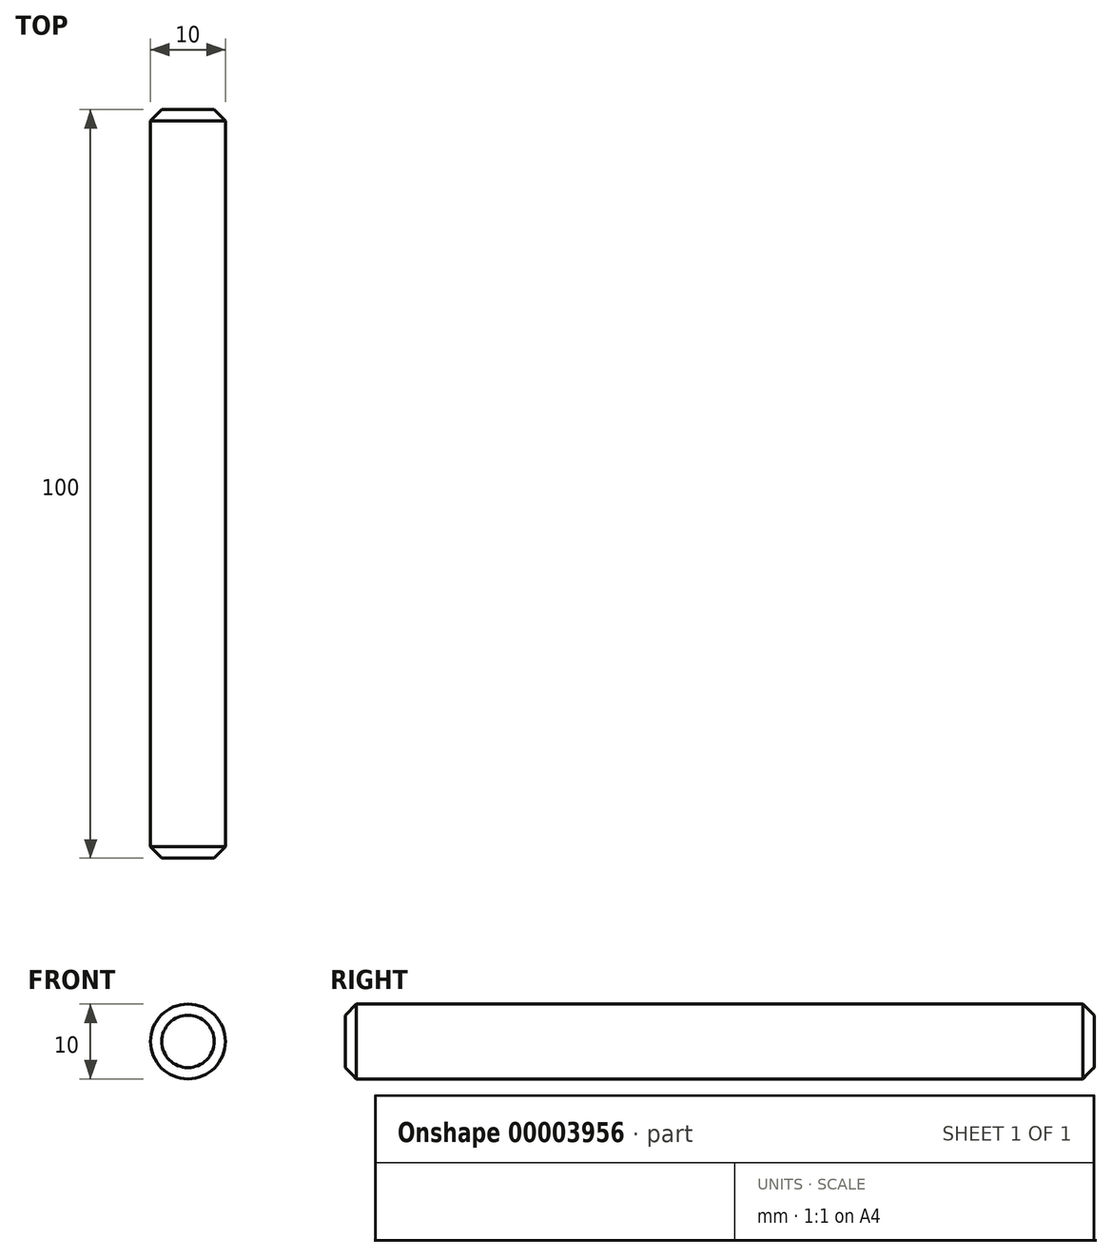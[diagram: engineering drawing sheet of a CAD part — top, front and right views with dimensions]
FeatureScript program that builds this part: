
annotation { "Feature Type Name" : "Feature", "Feature Type Description" : "" }
export const myFeature = defineFeature(function(context is Context, id is Id, definition is map)
    precondition{}
    {
        {
            var Q0;
            Q0=qCreatedBy(makeId("Front.planeOp"),FACE);
            var sketch = newSketch(context, id + "F0", { "sketchPlane" : qUnion([Q0])});
            skCircle(sketch, "E0", {"center": v(0, 0) * mm, "radius": 5 * mm});
            skSolve(sketch);
        }
        {
            var Q0;
            Q0=makeQuery(id+"F0.imprint","IMPRINT",FACE,{"disambiguationData":[TD([[makeQuery(id+"F0.imprint","IMPRINT",EDGE,{"derivedFrom":sQuery(id+"F0.wireOp",EDGE,"E0")}),1.0]])]});
            extrude(context, id + "F1", {"entities" : qUnion([Q0]), "depth" : 100 * mm});
        }
        {
            var Q0;
            Q0=makeQuery(id+"F1.opExtrude","CAP_EDGE",EDGE,{"disambiguationData":[OSD([sQuery(id+"F0.wireOp",EDGE,"E0")])],"isStart":false});
            var Q1;
            Q1=makeQuery(id+"F1.opExtrude","CAP_EDGE",EDGE,{"disambiguationData":[OSD([sQuery(id+"F0.wireOp",EDGE,"E0")])],"isStart":true});
            chamfer(context, id + "F2", {"entities" : qUnion([Q0, Q1]), "width" : 1.5 * mm, "tangentPropagation" : true});
        }
    });
